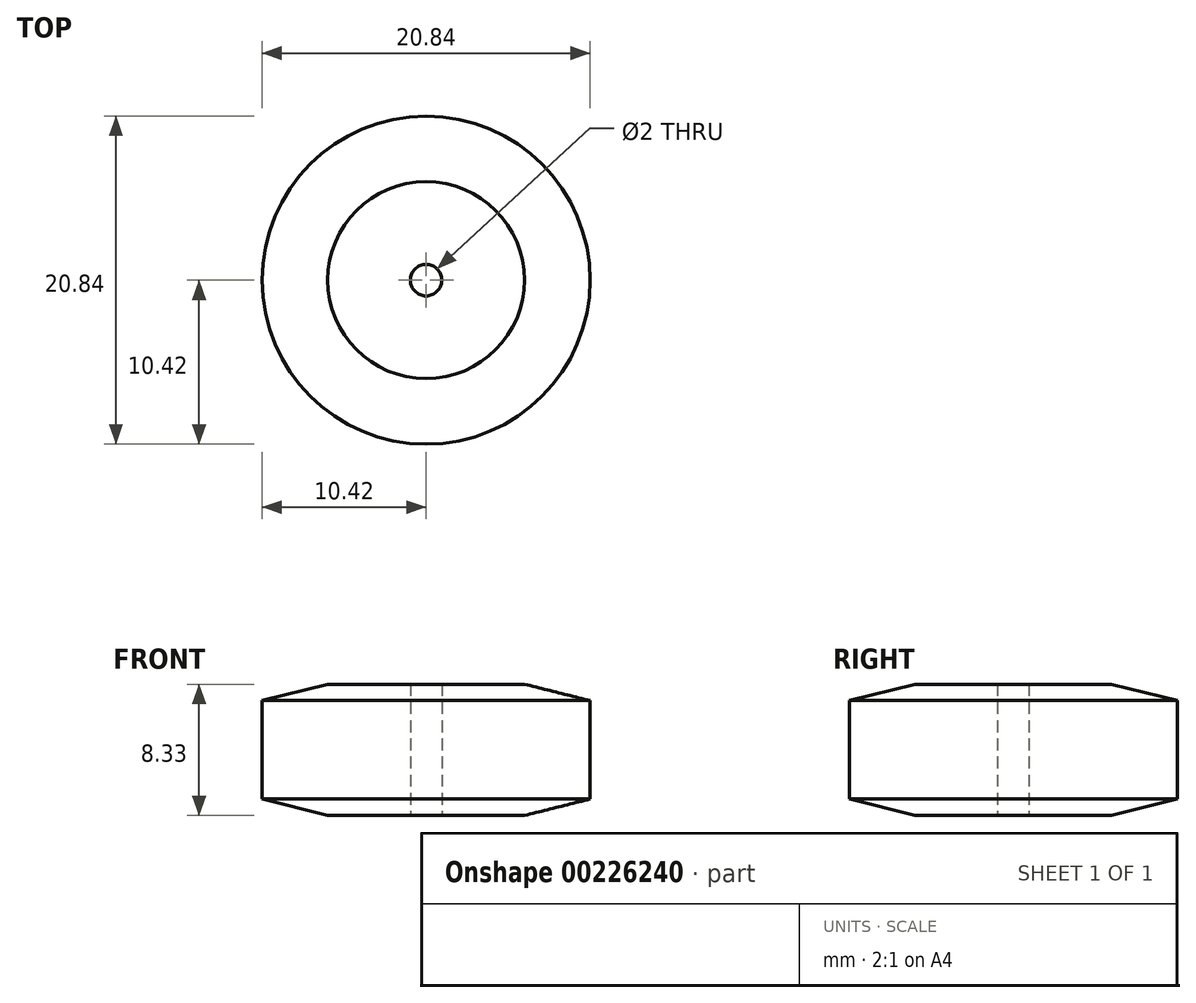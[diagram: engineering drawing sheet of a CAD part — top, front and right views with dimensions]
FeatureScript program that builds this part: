
annotation { "Feature Type Name" : "Feature", "Feature Type Description" : "" }
export const myFeature = defineFeature(function(context is Context, id is Id, definition is map)
    precondition{}
    {
        {
            var Q0;
            Q0=qCreatedBy(makeId("Top.planeOp"),FACE);
            var sketch = newSketch(context, id + "F0", { "sketchPlane" : qUnion([Q0])});
            skCircle(sketch, "E0", {"center": v(0, 0) * mm, "radius": 10.42 * mm});
            skCircle(sketch, "E1", {"center": v(0, 0) * mm, "radius": 1 * mm});
            skSolve(sketch);
        }
        {
            var Q0;
            Q0 = qSketchRegion(id + "F0", true);
            extrude(context, id + "F1", {"entities" : qUnion([Q0]), "depth" : 400 / 48 * mm});
        }
        {
            var Q0;
            Q0=makeQuery(id+"F1.opExtrude","CAP_EDGE",EDGE,{"disambiguationData":[OSD([sQuery(id+"F0.wireOp",EDGE,"E0")])],"isStart":false});
            chamfer(context, id + "F2", {"entities" : qUnion([Q0]), "chamferType" : ChamferType.TWO_OFFSETS, "width1" : 200 / 48 * mm, "oppositeDirection" : false, "width2" : 50 / 48 * mm, "tangentPropagation" : true});
        }
        {
            var Q0;
            Q0=makeQuery(id+"F1.opExtrude","CAP_EDGE",EDGE,{"disambiguationData":[OSD([sQuery(id+"F0.wireOp",EDGE,"E0")])],"isStart":true});
            chamfer(context, id + "F3", {"entities" : qUnion([Q0]), "chamferType" : ChamferType.TWO_OFFSETS, "width1" : 50 / 48 * mm, "oppositeDirection" : false, "width2" : 200 / 48 * mm, "tangentPropagation" : true});
        }
    });
